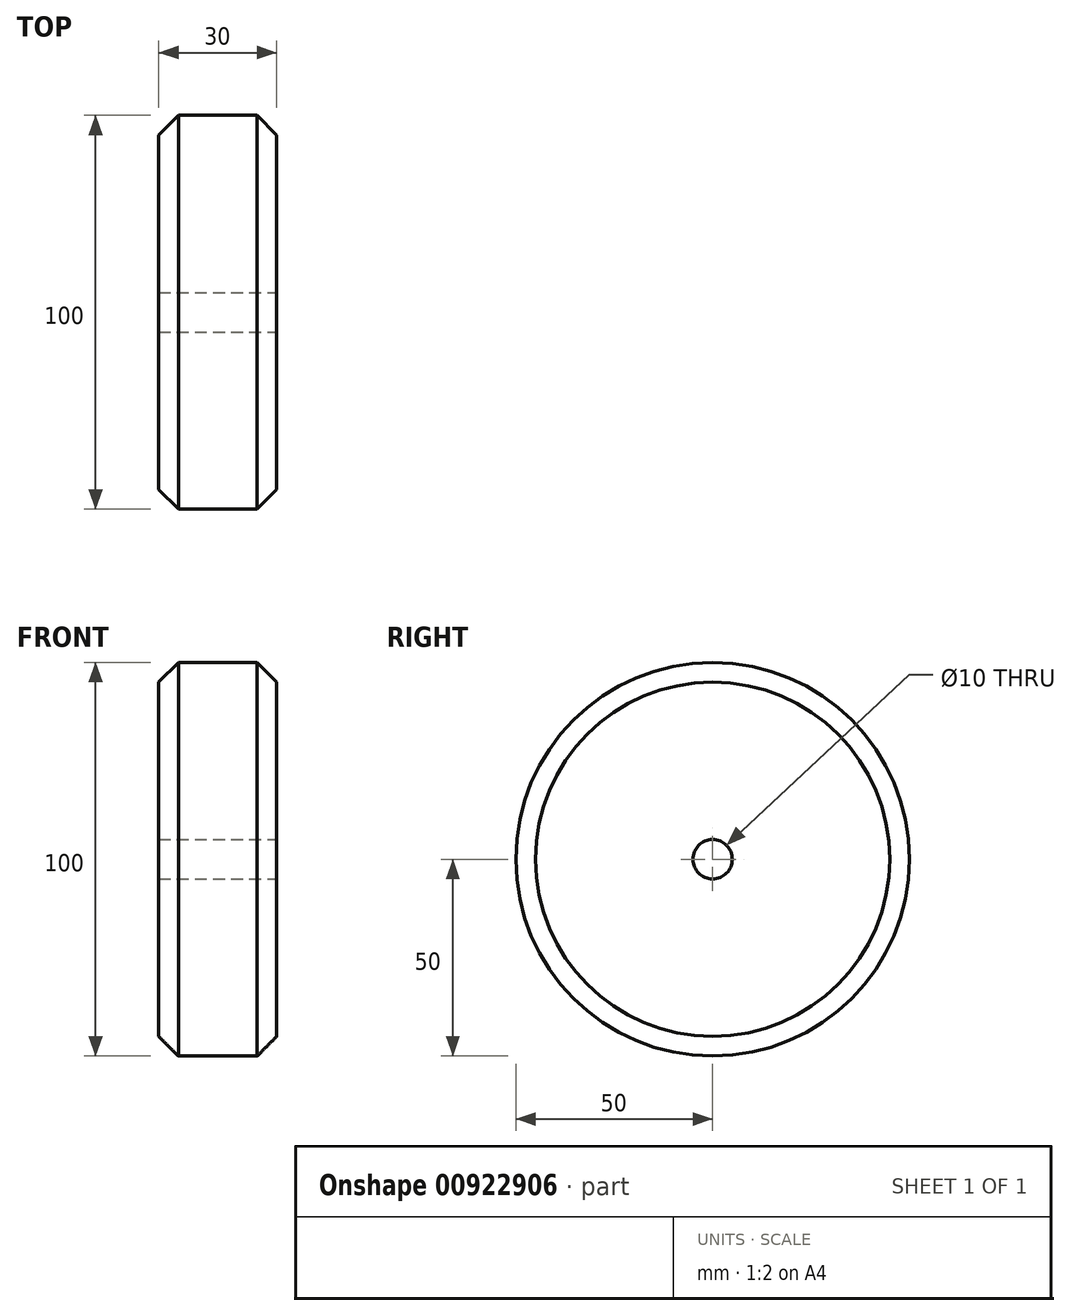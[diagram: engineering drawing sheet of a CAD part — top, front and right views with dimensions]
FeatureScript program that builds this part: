
annotation { "Feature Type Name" : "Feature", "Feature Type Description" : "" }
export const myFeature = defineFeature(function(context is Context, id is Id, definition is map)
    precondition{}
    {
        {
            var Q0;
            Q0=qCreatedBy(makeId("Top.planeOp"),FACE);
            var sketch = newSketch(context, id + "F0", { "sketchPlane" : qUnion([Q0])});
            skLineSegment(sketch, "E0.bottom", {"start": v(15, 5) * mm, "end": v(-15, 5) * mm});
            skLineSegment(sketch, "E0.top", {"start": v(15, 50) * mm, "end": v(-15, 50) * mm});
            skLineSegment(sketch, "E0.left", {"start": v(15, 5) * mm, "end": v(15, 50) * mm});
            skLineSegment(sketch, "E0.right", {"start": v(-15, 5) * mm, "end": v(-15, 50) * mm});
            skPoint(sketch, "E0.middle", {"position": v(0, 27.5) * mm});
            skLineSegment(sketch, "E1", {"start": v(0, 0) * mm, "end": v(-43.67, 0) * mm});
            skSolve(sketch);
        }
        {
            var Q0;
            Q0 = qSketchRegion(id + "F0", true);
            var Q1;
            Q1=sQuery(id+"F0.wireOp",EDGE,"E1");
            revolve(context, id + "F1", {"surfaceOperationType" : NewSurfaceOperationType.NEW, "entities" : qUnion([Q0]), "axis" : qUnion([Q1]), "revolveType" : RevolveType.FULL});
        }
        {
            var Q0;
            Q0=makeQuery(id+"F1.opRevolve","SWEPT_EDGE",EDGE,{"disambiguationData":[OSD([sQuery(id+"F0.wireOp",EDGE,"E0.top"),sQuery(id+"F0.wireOp",EDGE,"E0.left")])]});
            var Q1;
            Q1=makeQuery(id+"F1.opRevolve","SWEPT_EDGE",EDGE,{"disambiguationData":[OSD([sQuery(id+"F0.wireOp",EDGE,"E0.top"),sQuery(id+"F0.wireOp",EDGE,"E0.right")])]});
            chamfer(context, id + "F2", {"entities" : qUnion([Q0, Q1]), "width" : 5 * mm, "tangentPropagation" : true});
        }
    });
